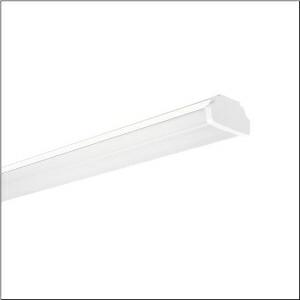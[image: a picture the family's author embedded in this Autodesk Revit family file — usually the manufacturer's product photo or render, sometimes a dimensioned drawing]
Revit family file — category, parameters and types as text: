
# Revit family: modario_r__31_ho_53bm811m1v4120_5d14
name_source: partatom
category: Lighting Fixtures
units: mm (PartAtom-declared; Revit-internal decimal feet)

## family parameters
Cut with Voids When Loaded = No
Host = Face
Light Source = No
Part Type = Normal
Room Calculation Point = No
Round Connector Dimension = Use Diameter
Shared = No

## types (1)
- --- (1 x LED, 12380 lm, 77.3 W, 4000K)
    Apparent Load = 77 VA
    CIE Flux Codes = 52 78 94 90 100
    Color Rendering = 80
    Color Temperature = 4000K
    Default Elevation = 1800 mm
    Description = Modario® 31 HO, luminaire insert, of sheet steel, coil coated, white, length: 1.495mm, width: 81mm, height: 82mm, 5x system unit, system units: 299mm, LED rated luminous flux: 12.380lm, light colour: 840, control gear: ON/OFF Multilumen, control gear: ECG Multilumen, with plug, 3-pole, with phase selection, mains connection: 220..240V, AC, 50/60Hz, rated input power: 77W, through-wiring accessed according to module size, primary optical cover: cover, of PMMA, light emission: direct distribution, primary light characteristic: symmetric, protection rating (complete): IP20, protection rating (LED compartment): IP50, insulation class (complete): insulation class I (protective earthing), certification: CE, ENEC, VDE, UKCA, impact resistance: IK03, permissible ambient temperature for indoor applications: -35..+35°C, corresponds to IFS (International Featured Standards) requirements for safety and quality in the food industry, reducing of maximum allowable ambient temperature of 5°C with ceiling mounting, packaging unit: 1 piece
    Height = 92 mm
    Lamp = 1 x LED
    Lamp Light Flux = 12380 lm
    Lamp Power = 77.3 W
    Lamp count = 1
    Length = 1495 mm
    Luminous efficacy = 160 lm/W
    Manufacturer = Siteco
    ModVariant = No
    Model = 53BM811M1V4120
    Mounting Place = Ceiling
    Mounting Type = Pendant
    Number of Poles = 1
    OnlyDefault = Yes
    Power Factor = 1
    Product Name = Modario® 31 HO
    Product group = luminaire insert
    ProductGroupID = 902
    Protection Class = Protection class I
    Protection Degree = IP 20
    RLX_Detail_Level = 1
    RLX_Emergency_Light_Flux = 0 lm
    RLX_Emergency_Type = 0
    RLX_Emergency_Type_DB = No
    RlxData = <blob elided: 40029 chars, md5=6cfb2e8f>
    Socket = socket
    Standby Power = 0 W
    System Light Flux = 12380 lm
    System Power = 77 W
    Type Comments = factory setting: luminous flux: 100 % | (A | C | E) | 173 mA
    Type Image = l_1341886.jpg
    URL = http://relux.com
    VarID = @adj_197384
    Voltage = 0 V
    Weight = 0.00 kg
    Width = 81 mm

## geometry (parser evidence)
native form markers: Blend x4, Sweep x12
no freeform markers — native parametric forms only
